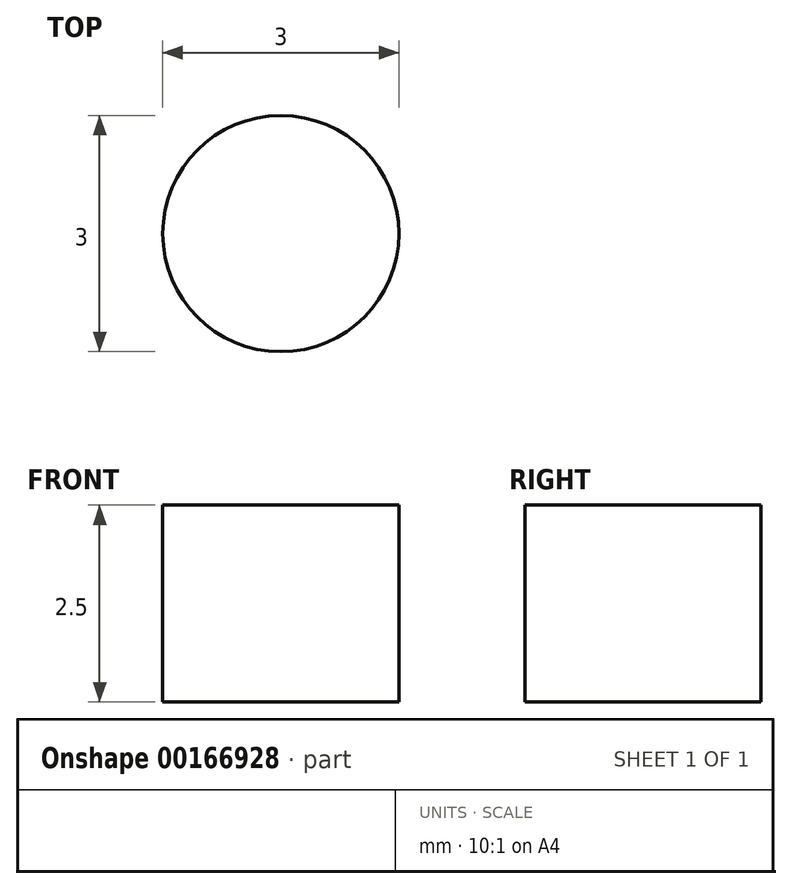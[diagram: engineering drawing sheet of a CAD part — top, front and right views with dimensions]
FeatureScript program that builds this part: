
annotation { "Feature Type Name" : "Feature", "Feature Type Description" : "" }
export const myFeature = defineFeature(function(context is Context, id is Id, definition is map)
    precondition{}
    {
        {
            var Q0;
            Q0=qCreatedBy(makeId("Top.planeOp"),FACE);
            var sketch = newSketch(context, id + "F0", { "sketchPlane" : qUnion([Q0])});
            skCircle(sketch, "E0", {"center": v(-138.25, 12) * mm, "radius": 1.5 * mm});
            skCircle(sketch, "E1", {"center": v(-128.25, 12) * mm, "radius": 1.5 * mm});
            skCircle(sketch, "E2", {"center": v(-138.25, -12) * mm, "radius": 1.5 * mm});
            skCircle(sketch, "E3", {"center": v(-128.25, -12) * mm, "radius": 1.5 * mm});
            skCircle(sketch, "E4", {"center": v(-112.25, -40) * mm, "radius": 2 * mm});
            skCircle(sketch, "E5", {"center": v(-112.25, 40) * mm, "radius": 2 * mm});
            skArc(sketch, "E6", {"start": v(-53.25, -59.5) * mm, "mid": v(-52.22, -61.97) * mm, "end": v(-49.75, -63) * mm});
            skLineSegment(sketch, "E7", {"start": v(-49.75, -63) * mm, "end": v(-39.75, -63) * mm});
            skArc(sketch, "E8", {"start": v(-39.75, -63) * mm, "mid": v(-37.28, -61.97) * mm, "end": v(-36.25, -59.5) * mm});
            skArc(sketch, "E9", {"start": v(-36.25, -59.5) * mm, "mid": v(-37.28, -57.03) * mm, "end": v(-39.75, -56) * mm});
            skLineSegment(sketch, "E10", {"start": v(-39.75, -56) * mm, "end": v(-49.75, -56) * mm});
            skArc(sketch, "E11", {"start": v(-49.75, -56) * mm, "mid": v(-52.22, -57.03) * mm, "end": v(-53.25, -59.5) * mm});
            skCircle(sketch, "E12", {"center": v(67.75, -45) * mm, "radius": 1.5 * mm});
            skCircle(sketch, "E13", {"center": v(58.75, -16) * mm, "radius": 1.5 * mm});
            skCircle(sketch, "E14", {"center": v(97.75, -16) * mm, "radius": 1.5 * mm});
            skCircle(sketch, "E15", {"center": v(91.75, -44) * mm, "radius": 2 * mm});
            skCircle(sketch, "E16", {"center": v(97.75, 16) * mm, "radius": 1.5 * mm});
            skCircle(sketch, "E17", {"center": v(91.75, 44) * mm, "radius": 2 * mm});
            skCircle(sketch, "E18", {"center": v(67.75, 45) * mm, "radius": 1.5 * mm});
            skCircle(sketch, "E19", {"center": v(58.75, 16) * mm, "radius": 1.5 * mm});
            skCircle(sketch, "E20", {"center": v(75.75, 0) * mm, "radius": 7.5 * mm});
            skCircle(sketch, "E21", {"center": v(-12.75, -45) * mm, "radius": 1.5 * mm});
            skCircle(sketch, "E22", {"center": v(-12.75, 45) * mm, "radius": 1.5 * mm});
            skArc(sketch, "E23", {"start": v(-25.75, 25) * mm, "mid": v(-25.02, 23.23) * mm, "end": v(-23.25, 22.5) * mm});
            skLineSegment(sketch, "E24", {"start": v(-23.25, 22.5) * mm, "end": v(-13.75, 22.5) * mm});
            skArc(sketch, "E25", {"start": v(-13.75, 22.5) * mm, "mid": v(-11.98, 23.23) * mm, "end": v(-11.25, 25) * mm});
            skArc(sketch, "E26", {"start": v(-11.25, 25) * mm, "mid": v(-11.98, 26.77) * mm, "end": v(-13.75, 27.5) * mm});
            skLineSegment(sketch, "E27", {"start": v(-13.75, 27.5) * mm, "end": v(-23.25, 27.5) * mm});
            skArc(sketch, "E28", {"start": v(-23.25, 27.5) * mm, "mid": v(-25.02, 26.77) * mm, "end": v(-25.75, 25) * mm});
            skArc(sketch, "E29", {"start": v(10.25, 25) * mm, "mid": v(10.98, 23.23) * mm, "end": v(12.75, 22.5) * mm});
            skLineSegment(sketch, "E30", {"start": v(12.75, 22.5) * mm, "end": v(22.25, 22.5) * mm});
            skArc(sketch, "E31", {"start": v(22.25, 22.5) * mm, "mid": v(24.02, 23.23) * mm, "end": v(24.75, 25) * mm});
            skArc(sketch, "E32", {"start": v(24.75, 25) * mm, "mid": v(24.02, 26.77) * mm, "end": v(22.25, 27.5) * mm});
            skLineSegment(sketch, "E33", {"start": v(22.25, 27.5) * mm, "end": v(12.75, 27.5) * mm});
            skArc(sketch, "E34", {"start": v(12.75, 27.5) * mm, "mid": v(10.98, 26.77) * mm, "end": v(10.25, 25) * mm});
            skArc(sketch, "E35", {"start": v(-25.75, -25) * mm, "mid": v(-25.02, -26.77) * mm, "end": v(-23.25, -27.5) * mm});
            skLineSegment(sketch, "E36", {"start": v(-23.25, -27.5) * mm, "end": v(-13.75, -27.5) * mm});
            skArc(sketch, "E37", {"start": v(-13.75, -27.5) * mm, "mid": v(-11.98, -26.77) * mm, "end": v(-11.25, -25) * mm});
            skArc(sketch, "E38", {"start": v(-11.25, -25) * mm, "mid": v(-11.98, -23.23) * mm, "end": v(-13.75, -22.5) * mm});
            skLineSegment(sketch, "E39", {"start": v(-13.75, -22.5) * mm, "end": v(-23.25, -22.5) * mm});
            skArc(sketch, "E40", {"start": v(-23.25, -22.5) * mm, "mid": v(-25.02, -23.23) * mm, "end": v(-25.75, -25) * mm});
            skArc(sketch, "E41", {"start": v(10.25, -25) * mm, "mid": v(10.98, -26.77) * mm, "end": v(12.75, -27.5) * mm});
            skLineSegment(sketch, "E42", {"start": v(12.75, -27.5) * mm, "end": v(22.25, -27.5) * mm});
            skArc(sketch, "E43", {"start": v(22.25, -27.5) * mm, "mid": v(24.02, -26.77) * mm, "end": v(24.75, -25) * mm});
            skArc(sketch, "E44", {"start": v(24.75, -25) * mm, "mid": v(24.02, -23.23) * mm, "end": v(22.25, -22.5) * mm});
            skLineSegment(sketch, "E45", {"start": v(22.25, -22.5) * mm, "end": v(12.75, -22.5) * mm});
            skArc(sketch, "E46", {"start": v(12.75, -22.5) * mm, "mid": v(10.98, -23.23) * mm, "end": v(10.25, -25) * mm});
            skCircle(sketch, "E47", {"center": v(-71, 43) * mm, "radius": 1.5 * mm});
            skCircle(sketch, "E48", {"center": v(-71, -43) * mm, "radius": 1.5 * mm});
            skCircle(sketch, "E49", {"center": v(20.5, -51.5) * mm, "radius": 1.5 * mm});
            skCircle(sketch, "E50", {"center": v(38.5, -51.5) * mm, "radius": 1.5 * mm});
            skCircle(sketch, "E51", {"center": v(134, 40) * mm, "radius": 2 * mm});
            skCircle(sketch, "E52", {"center": v(134, -40) * mm, "radius": 2 * mm});
            skLineSegment(sketch, "E53", {"start": v(-148.25, 24.5) * mm, "end": v(-115.92, 58.73) * mm});
            skArc(sketch, "E54", {"start": v(-115.92, 58.73) * mm, "mid": v(-109.3, 63.37) * mm, "end": v(-101.38, 65) * mm});
            skLineSegment(sketch, "E55", {"start": v(-101.38, 65) * mm, "end": v(-17.75, 65) * mm});
            skLineSegment(sketch, "E56", {"start": v(-17.75, 65) * mm, "end": v(145.97, 50.2) * mm});
            skArc(sketch, "E57", {"start": v(145.97, 50.2) * mm, "mid": v(147.6, 49.4) * mm, "end": v(148.25, 47.72) * mm});
            skLineSegment(sketch, "E58", {"start": v(148.25, 47.72) * mm, "end": v(148.25, -36.5) * mm});
            skLineSegment(sketch, "E59", {"start": v(148.25, -36.5) * mm, "end": v(148.25, -47.72) * mm});
            skArc(sketch, "E60", {"start": v(148.25, -47.72) * mm, "mid": v(147.6, -49.4) * mm, "end": v(145.97, -50.2) * mm});
            skLineSegment(sketch, "E61", {"start": v(145.97, -50.2) * mm, "end": v(-17.75, -65) * mm});
            skLineSegment(sketch, "E62", {"start": v(-17.75, -65) * mm, "end": v(-101.38, -65) * mm});
            skArc(sketch, "E63", {"start": v(-101.38, -65) * mm, "mid": v(-109.3, -63.37) * mm, "end": v(-115.92, -58.73) * mm});
            skLineSegment(sketch, "E64", {"start": v(-115.92, -58.73) * mm, "end": v(-148.25, -24.5) * mm});
            skLineSegment(sketch, "E65", {"start": v(-148.25, -24.5) * mm, "end": v(-148.25, 24.5) * mm});
            skLineSegment(sketch, "E66", {"start": v(-104.25, 31.5) * mm, "end": v(-99.48, 39.3) * mm});
            skLineSegment(sketch, "E67", {"start": v(-99.48, 39.3) * mm, "end": v(-97.35, 40.5) * mm});
            skLineSegment(sketch, "E68", {"start": v(-97.35, 40.5) * mm, "end": v(-87.75, 40.5) * mm});
            skLineSegment(sketch, "E69", {"start": v(-87.75, 40.5) * mm, "end": v(-85.25, 38) * mm});
            skLineSegment(sketch, "E70", {"start": v(-85.25, 38) * mm, "end": v(-82.75, 35.5) * mm});
            skLineSegment(sketch, "E71", {"start": v(-82.75, 35.5) * mm, "end": v(-34, 35.5) * mm});
            skLineSegment(sketch, "E72", {"start": v(-34, 35.5) * mm, "end": v(-28, 29.5) * mm});
            skLineSegment(sketch, "E73", {"start": v(-28, 29.5) * mm, "end": v(-28, 24) * mm});
            skLineSegment(sketch, "E74", {"start": v(-28, 24) * mm, "end": v(-23, 19) * mm});
            skLineSegment(sketch, "E75", {"start": v(-23, 19) * mm, "end": v(5.25, 19) * mm});
            skLineSegment(sketch, "E76", {"start": v(5.25, 19) * mm, "end": v(24, 0.25) * mm});
            skLineSegment(sketch, "E77", {"start": v(24, 0.25) * mm, "end": v(24, -0.25) * mm});
            skLineSegment(sketch, "E78", {"start": v(24, -0.25) * mm, "end": v(5.25, -19) * mm});
            skLineSegment(sketch, "E79", {"start": v(5.25, -19) * mm, "end": v(-23, -19) * mm});
            skLineSegment(sketch, "E80", {"start": v(-23, -19) * mm, "end": v(-28, -24) * mm});
            skLineSegment(sketch, "E81", {"start": v(-28, -24) * mm, "end": v(-28, -30) * mm});
            skLineSegment(sketch, "E82", {"start": v(-28, -30) * mm, "end": v(-25, -33) * mm});
            skLineSegment(sketch, "E83", {"start": v(-25, -33) * mm, "end": v(-24.25, -33) * mm});
            skLineSegment(sketch, "E84", {"start": v(-24.25, -33) * mm, "end": v(-20.75, -36.5) * mm});
            skLineSegment(sketch, "E85", {"start": v(-20.75, -36.5) * mm, "end": v(-24.25, -40) * mm});
            skLineSegment(sketch, "E86", {"start": v(-24.25, -40) * mm, "end": v(-70.75, -40) * mm});
            skLineSegment(sketch, "E87", {"start": v(-70.75, -40) * mm, "end": v(-73, -39) * mm});
            skLineSegment(sketch, "E88", {"start": v(-73, -39) * mm, "end": v(-96.75, -39) * mm});
            skArc(sketch, "E89", {"start": v(-106.4, -31.14) * mm, "mid": v(-102.97, -36.78) * mm, "end": v(-96.75, -39) * mm});
            skArc(sketch, "E90", {"start": v(-106.6, 25.8) * mm, "mid": v(-107.8, -2.68) * mm, "end": v(-106.4, -31.14) * mm});
            skArc(sketch, "E91", {"start": v(-104.25, 31.5) * mm, "mid": v(-105.75, 28.78) * mm, "end": v(-106.6, 25.8) * mm});
            skSolve(sketch);
        }
        {
            var Q0;
            Q0=makeQuery(id+"F0.imprint","IMPRINT",FACE,{"disambiguationData":[TD([[makeQuery(id+"F0.imprint","IMPRINT",EDGE,{"derivedFrom":sQuery(id+"F0.wireOp",EDGE,"E0")}),1.0]])]});
            extrude(context, id + "F1", {"entities" : qUnion([Q0]), "depth" : 2.5 * mm});
        }
    });
